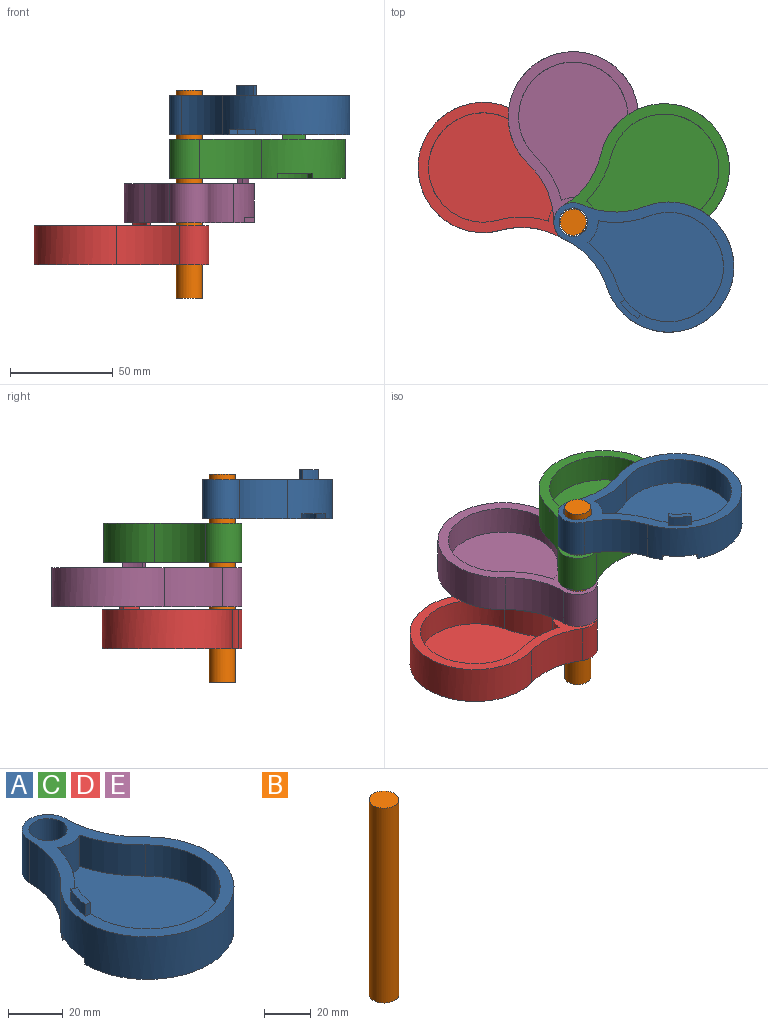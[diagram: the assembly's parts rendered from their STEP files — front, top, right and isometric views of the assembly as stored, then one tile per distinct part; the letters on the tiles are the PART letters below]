
ASSEMBLY  parts=5 mates=4
PART A: 24 faces, bbox 63.5x92.7x24.1 mm
  f0: cylinder r=26.67mm len=4.64mm, axis (0,0,-1), area 15.5mm2, adj f7,f17,f21,f23
  f1: plane 92.71x63.5mm, normal (0,0,1), area 1127.8mm2, adj f2,f3,f4,f5,f6,f8,f9,f10
  f2: cylinder r=31.75mm len=63.5mm, axis (0,0,-1), area 2842.5mm2, adj f1,f3,f5,f7,f21,f22,f23
  f3: cylinder r=38.88mm len=28.31mm, axis (0,0,-1), area 604.2mm2, adj f1,f2,f4,f7
  f4: cylinder r=9.53mm len=19.05mm, axis (0,0,-1), area 570mm2, adj f1,f3,f5,f7
  f5: cylinder r=38.88mm len=28.31mm, axis (0,0,-1), area 604.2mm2, adj f1,f2,f4,f7
  f6: cylinder r=6.99mm len=19.05mm, axis (0,0,-1), area 836.1mm2, adj f1,f7
  f7: plane 92.71x63.5mm, normal (0,0,-1), area 1071.6mm2, adj f0,f2,f3,f4,f5,f6,f17,f18
  f8: cylinder r=26.67mm len=53.34mm, axis (0,0,-1), area 1831.3mm2, adj f1,f9,f10,f12,f14,f15,f16
  f9: cylinder r=43.96mm len=21.4mm, axis (0,0,-1), area 351.3mm2, adj f1,f8,f11,f12
  f10: cylinder r=43.96mm len=21.4mm, axis (0,0,-1), area 351.3mm2, adj f1,f8,f11,f12
  f11: cylinder r=12.06mm len=13.97mm, axis (0,0,-1), area 167.3mm2, adj f1,f9,f10,f12
  f12: plane 67.5x53.34mm, normal (0,0,1), area 2496.1mm2, adj f8,f9,f10,f11
  f13: cylinder r=29.21mm len=10.86mm, axis (0,0,-1), area 58mm2, adj f1,f14,f15,f16
  f14: plane 5.08x2.53mm, normal (-0.1,-0.99,0), area 12.9mm2, adj f1,f8,f13,f16
  f15: plane 5.08x2.24mm, normal (0.47,0.88,0), area 12.9mm2, adj f1,f8,f13,f16
  f16: plane 11.11x5.56mm, normal (0,0,1), area 27.8mm2, adj f8,f13,f14,f15
  f17: cylinder r=43.96mm len=21.4mm, axis (0,0,-1), area 63.9mm2, adj f0,f7,f18,f21
  f18: cylinder r=12.06mm len=11.49mm, axis (0,0,-1), area 30.4mm2, adj f7,f17,f19,f21
  f19: cylinder r=43.96mm len=21.4mm, axis (0,0,-1), area 63.9mm2, adj f7,f18,f20,f21
  f20: cylinder r=26.67mm len=53.34mm, axis (0,0,-1), area 268.5mm2, adj f7,f19,f21,f22
  f21: plane 67.5x58.41mm, normal (0,0,-1), area 2580mm2, adj f0,f2,f17,f18,f19,f20,f22,f23
  f22: plane 5.07x2.54mm, normal (0.1,0.99,0), area 13mm2, adj f2,f7,f20,f21
  f23: plane 4.49x2.54mm, normal (-0.47,-0.88,0), area 13mm2, adj f0,f2,f7,f21
PART B: 3 faces, bbox 12.7x12.7x101.6 mm
  f0: cylinder r=6.35mm len=101.6mm, axis (0,0,-1), area 4053.7mm2, adj f1,f2
  f1: plane 12.7x12.7mm, normal (0,0,1), area 126.7mm2, adj f0
  f2: plane 12.7x12.7mm, normal (0,0,-1), area 126.7mm2, adj f0
PART C: same geometry as A
PART D: same geometry as A
PART E: same geometry as A
PLACE A rot(axis=(0,0,1),64.8deg) t=(46.54,-21.9,79.71)mm
PLACE B at identity
PLACE C rot(axis=(0,0,1),120.4deg) t=(44.35,26.06,58.62)mm
PLACE D rot(axis=(0,0,-1),121.4deg) t=(-43.92,26.76,16.47)mm
PLACE E rot(axis=(0,0,-1),180deg) t=(-0.01,51.43,36.99)mm
MATE cylindrical C.f6 <-> B.f0  axis (0,0,-1) through (0,0,77.67)mm
MATE cylindrical A.f6 <-> B.f0  axis (0,0,1) through (0,0,84.79)mm
MATE cylindrical E.f4 <-> B.f0  axis (0,0,1) through (0,0,56.04)mm
MATE cylindrical B.f0 <-> D.f6  axis (0,0,1) through (0,0,101.6)mm
